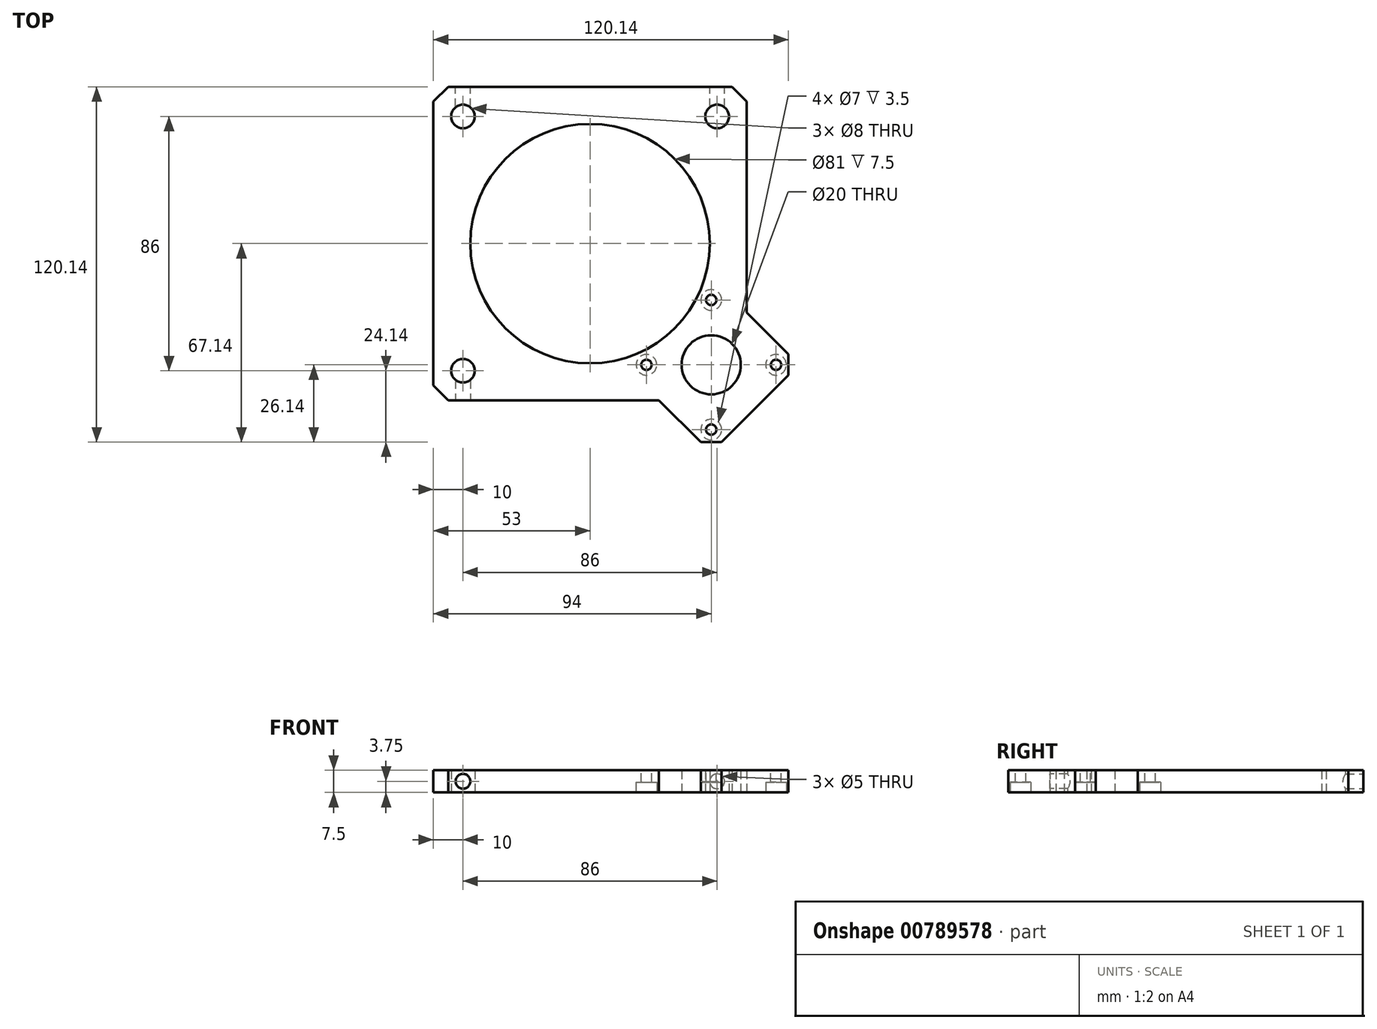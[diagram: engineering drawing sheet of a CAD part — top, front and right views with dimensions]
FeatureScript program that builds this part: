
annotation { "Feature Type Name" : "Feature", "Feature Type Description" : "" }
export const myFeature = defineFeature(function(context is Context, id is Id, definition is map)
    precondition{}
    {
        {
            var Q0;
            Q0=qCreatedBy(makeId("Top.planeOp"),FACE);
            var sketch = newSketch(context, id + "F0", { "sketchPlane" : qUnion([Q0])});
            skPoint(sketch, "E0.middle", {"position": v(0, 0) * mm});
            skCircle(sketch, "E1", {"center": v(0, 0) * mm, "radius": 40.5 * mm});
            skCircle(sketch, "E2", {"center": v(43, 43) * mm, "radius": 4 * mm});
            skCircle(sketch, "E3", {"center": v(-43, -43) * mm, "radius": 4 * mm});
            skLineSegment(sketch, "E4", {"start": v(41, -70.68) * mm, "end": v(41, -41) * mm});
            skCircle(sketch, "E5", {"center": v(41, -41) * mm, "radius": 10 * mm});
            skCircle(sketch, "E6", {"center": v(-43, 43) * mm, "radius": 4 * mm});
            skLineSegment(sketch, "E7", {"start": v(-53, 53) * mm, "end": v(-53, -53) * mm});
            skLineSegment(sketch, "E8", {"start": v(-53, -53) * mm, "end": v(23.32, -53) * mm});
            skLineSegment(sketch, "E9", {"start": v(-53, 53) * mm, "end": v(53, 53) * mm});
            skLineSegment(sketch, "E10", {"start": v(53, 53) * mm, "end": v(53, -23.32) * mm});
            skLineSegment(sketch, "E11", {"start": v(23.32, -53) * mm, "end": v(41, -70.68) * mm});
            skLineSegment(sketch, "E12", {"start": v(53, -23.32) * mm, "end": v(70.68, -41) * mm});
            skLineSegment(sketch, "E13", {"start": v(70.68, -41) * mm, "end": v(41, -70.68) * mm});
            skPoint(sketch, "E14.end.orphan", {"position": v(41, -70.68) * mm});
            skSolve(sketch);
        }
        {
            var Q0;
            Q0=makeQuery(id+"F0.imprint","IMPRINT",FACE,{"disambiguationData":[TD([[makeQuery(id+"F0.imprint","IMPRINT",EDGE,{"derivedFrom":sQuery(id+"F0.wireOp",EDGE,"E1")}),-1.0]])]});
            var Q1;
            {var subQ1=sQuery(id+"F0.wireOp",EDGE,"E0.left");var subQ6=sQuery(id+"F0.wireOp",EDGE,"E0.bottom");var subQ9=makeQuery(id+"F0.imprint","INTERSECT",VERTEX,{"derivedFrom":[subQ6,subQ1]});Q1=makeQuery(id+"F0.imprint","IMPRINT",FACE,{"disambiguationData":[TD([[makeQuery(id+"F0.imprint","IMPRINT",EDGE,{"disambiguationData":[TD([[subQ9,-1.0]])],"derivedFrom":subQ6}),1.0]])]});}
            var Q2;
            {var subQ1=sQuery(id+"F0.wireOp",EDGE,"E0.right");var subQ6=sQuery(id+"F0.wireOp",EDGE,"E0.top");var subQ9=makeQuery(id+"F0.imprint","INTERSECT",VERTEX,{"derivedFrom":[subQ6,subQ1]});Q2=makeQuery(id+"F0.imprint","IMPRINT",FACE,{"disambiguationData":[TD([[makeQuery(id+"F0.imprint","IMPRINT",EDGE,{"disambiguationData":[TD([[subQ9,1.0]])],"derivedFrom":subQ6}),-1.0]])]});}
            var Q3;
            {var subQ1=sQuery(id+"F0.wireOp",EDGE,"E0.right");var subQ6=sQuery(id+"F0.wireOp",EDGE,"E0.bottom");var subQ9=makeQuery(id+"F0.imprint","INTERSECT",VERTEX,{"derivedFrom":[subQ6,subQ1]});Q3=makeQuery(id+"F0.imprint","IMPRINT",FACE,{"disambiguationData":[TD([[makeQuery(id+"F0.imprint","IMPRINT",EDGE,{"disambiguationData":[TD([[subQ9,1.0]])],"derivedFrom":subQ6}),1.0]])]});}
            var Q4;
            {var subQ1=sQuery(id+"F0.wireOp",EDGE,"0d9eabcc-9e13-4dd9-8463-7bf05dad1fff");var subQ11=sQuery(id+"F0.wireOp",EDGE,"E0.bottom");var subQ18=makeQuery(id+"F0.imprint","INTERSECT",VERTEX,{"derivedFrom":[subQ11,subQ1]});Q4=makeQuery(id+"F0.imprint","IMPRINT",FACE,{"disambiguationData":[TD([[makeQuery(id+"F0.imprint","IMPRINT",EDGE,{"disambiguationData":[TD([[subQ18,-1.0]])],"derivedFrom":subQ11}),1.0]])]});}
            var Q5;
            {var subQ0=sQuery(id+"F0.wireOp",EDGE,"E0.left");var subQ1=sQuery(id+"F0.wireOp",EDGE,"E0.top");var subQ2=makeQuery(id+"F0.imprint","INTERSECT",VERTEX,{"derivedFrom":[subQ1,subQ0]});Q5=makeQuery(id+"F0.imprint","IMPRINT",FACE,{"disambiguationData":[TD([[makeQuery(id+"F0.imprint","IMPRINT",EDGE,{"disambiguationData":[TD([[subQ2,-1.0]])],"derivedFrom":subQ1}),-1.0]])]});}
            extrude(context, id + "F1", {"entities" : qUnion([Q0, Q1, Q2, Q3, Q4, Q5]), "depth" : 7.5 * mm, "offsetDistance" : 25 * mm});
        }
        {
            var Q0;
            Q0=makeQuery(id+"F1.opExtrude","CAP_FACE",FACE,{"disambiguationData":[OSD([sQuery(id+"F0.wireOp",EDGE,"E0.bottom"),sQuery(id+"F0.wireOp",EDGE,"E0.top"),sQuery(id+"F0.wireOp",EDGE,"E0.left"),sQuery(id+"F0.wireOp",EDGE,"E0.right"),sQuery(id+"F0.wireOp",EDGE,"E1"),sQuery(id+"F0.wireOp",EDGE,"E2"),sQuery(id+"F0.wireOp",EDGE,"E3"),sQuery(id+"F0.wireOp",EDGE,"E5"),sQuery(id+"F0.wireOp",EDGE,"E6")])],"isStart":false});
            var sketch = newSketch(context, id + "F2", { "sketchPlane" : qUnion([Q0])});
            skPoint(sketch, "E15", {"position": v(41, -41) * mm});
            skPoint(sketch, "E16", {"position": v(41, -19.08) * mm});
            skLineSegment(sketch, "E17", {"start": v(41, -19.08) * mm, "end": v(19.08, -41) * mm});
            skLineSegment(sketch, "E18", {"start": v(41, -41) * mm, "end": v(30.04, -30.04) * mm});
            skLineSegment(sketch, "E19", {"start": v(41, -41) * mm, "end": v(51.96, -51.96) * mm});
            skLineSegment(sketch, "E20", {"start": v(51.96, -51.96) * mm, "end": v(62.92, -41) * mm});
            skLineSegment(sketch, "E21", {"start": v(51.96, -51.96) * mm, "end": v(41, -62.92) * mm});
            skCircle(sketch, "E22", {"center": v(41, -19.08) * mm, "radius": 1.75 * mm});
            skCircle(sketch, "E23", {"center": v(62.92, -41) * mm, "radius": 1.75 * mm});
            skCircle(sketch, "E24", {"center": v(19.08, -41) * mm, "radius": 1.75 * mm});
            skCircle(sketch, "E25", {"center": v(41, -62.92) * mm, "radius": 1.75 * mm});
            skCircle(sketch, "E26", {"center": v(19.08, -41) * mm, "radius": 2.75 * mm});
            skCircle(sketch, "E27", {"center": v(41, -19.08) * mm, "radius": 2.75 * mm});
            skCircle(sketch, "E28", {"center": v(41, -62.92) * mm, "radius": 2.75 * mm});
            skCircle(sketch, "E29", {"center": v(62.92, -41) * mm, "radius": 2.75 * mm});
            skSolve(sketch);
        }
        {
            var Q0;
            Q0=makeQuery(id+"F2.imprint","IMPRINT",FACE,{"disambiguationData":[TD([[makeQuery(id+"F2.imprint","IMPRINT",EDGE,{"derivedFrom":sQuery(id+"F2.wireOp",EDGE,"E22")}),1.0]])]});
            var Q1;
            Q1=makeQuery(id+"F2.imprint","IMPRINT",FACE,{"disambiguationData":[TD([[makeQuery(id+"F2.imprint","IMPRINT",EDGE,{"derivedFrom":sQuery(id+"F2.wireOp",EDGE,"E24")}),1.0]])]});
            var Q2;
            Q2=makeQuery(id+"F2.imprint","IMPRINT",FACE,{"disambiguationData":[TD([[makeQuery(id+"F2.imprint","IMPRINT",EDGE,{"derivedFrom":sQuery(id+"F2.wireOp",EDGE,"E25")}),1.0]])]});
            var Q3;
            Q3=makeQuery(id+"F2.imprint","IMPRINT",FACE,{"disambiguationData":[TD([[makeQuery(id+"F2.imprint","IMPRINT",EDGE,{"derivedFrom":sQuery(id+"F2.wireOp",EDGE,"E23")}),1.0]])]});
            extrude(context, id + "F3", {"entities" : qUnion([Q0, Q1, Q2, Q3]), "operationType" : NewBodyOperationType.REMOVE, "oppositeDirection" : true, "depth" : 25 * mm, "offsetDistance" : 25 * mm});
        }
        {
            var Q0;
            Q0=makeQuery(id+"F1.opExtrude","CAP_FACE",FACE,{"disambiguationData":[OSD([sQuery(id+"F0.wireOp",EDGE,"E0.bottom"),sQuery(id+"F0.wireOp",EDGE,"E0.top"),sQuery(id+"F0.wireOp",EDGE,"E0.left"),sQuery(id+"F0.wireOp",EDGE,"E0.right"),sQuery(id+"F0.wireOp",EDGE,"E1"),sQuery(id+"F0.wireOp",EDGE,"E2"),sQuery(id+"F0.wireOp",EDGE,"E3"),sQuery(id+"F0.wireOp",EDGE,"E5"),sQuery(id+"F0.wireOp",EDGE,"E6")])],"isStart":true});
            var sketch = newSketch(context, id + "F4", { "sketchPlane" : qUnion([Q0])});
            skPoint(sketch, "E30", {"position": v(41, 41) * mm});
            skPoint(sketch, "E31", {"position": v(41, 62.92) * mm});
            skLineSegment(sketch, "E32", {"start": v(41, 62.92) * mm, "end": v(19.08, 41) * mm});
            skLineSegment(sketch, "E33", {"start": v(41, 41) * mm, "end": v(30.04, 51.96) * mm});
            skLineSegment(sketch, "E34", {"start": v(41, 41) * mm, "end": v(51.96, 30.04) * mm});
            skLineSegment(sketch, "E35", {"start": v(51.96, 30.04) * mm, "end": v(62.92, 41) * mm});
            skLineSegment(sketch, "E36", {"start": v(51.96, 30.04) * mm, "end": v(41, 19.08) * mm});
            skCircle(sketch, "E37", {"center": v(41, 62.92) * mm, "radius": 1.75 * mm});
            skCircle(sketch, "E38", {"center": v(62.92, 41) * mm, "radius": 1.75 * mm});
            skCircle(sketch, "E39", {"center": v(19.08, 41) * mm, "radius": 1.75 * mm});
            skCircle(sketch, "E40", {"center": v(41, 19.08) * mm, "radius": 1.75 * mm});
            skCircle(sketch, "E41", {"center": v(19.08, 41) * mm, "radius": 3.5 * mm});
            skCircle(sketch, "E42", {"center": v(41, 62.92) * mm, "radius": 3.5 * mm});
            skCircle(sketch, "E43", {"center": v(41, 19.08) * mm, "radius": 3.5 * mm});
            skCircle(sketch, "E44", {"center": v(62.92, 41) * mm, "radius": 3.5 * mm});
            skSolve(sketch);
        }
        {
            var Q0;
            Q0=makeQuery(id+"F4.imprint","IMPRINT",FACE,{"disambiguationData":[TD([[makeQuery(id+"F4.imprint","IMPRINT",EDGE,{"derivedFrom":sQuery(id+"F4.wireOp",EDGE,"E41")}),1.0]])]});
            var Q1;
            Q1=makeQuery(id+"F4.imprint","IMPRINT",FACE,{"disambiguationData":[TD([[makeQuery(id+"F4.imprint","IMPRINT",EDGE,{"derivedFrom":sQuery(id+"F4.wireOp",EDGE,"E42")}),1.0]])]});
            var Q2;
            Q2=makeQuery(id+"F4.imprint","IMPRINT",FACE,{"disambiguationData":[TD([[makeQuery(id+"F4.imprint","IMPRINT",EDGE,{"derivedFrom":sQuery(id+"F4.wireOp",EDGE,"E44")}),1.0]])]});
            var Q3;
            Q3=makeQuery(id+"F4.imprint","IMPRINT",FACE,{"disambiguationData":[TD([[makeQuery(id+"F4.imprint","IMPRINT",EDGE,{"derivedFrom":sQuery(id+"F4.wireOp",EDGE,"E40")}),1.0]])]});
            extrude(context, id + "F5", {"entities" : qUnion([Q0, Q1, Q2, Q3]), "operationType" : NewBodyOperationType.REMOVE, "oppositeDirection" : true, "depth" : 3.5 * mm, "offsetDistance" : 25 * mm});
        }
        {
            var Q0;
            Q0=makeQuery(id+"F1.opExtrude","SWEPT_FACE",FACE,{"disambiguationData":[OSD([sQuery(id+"F0.wireOp",EDGE,"E9")])]});
            var sketch = newSketch(context, id + "F6", { "sketchPlane" : qUnion([Q0])});
            skPoint(sketch, "E45", {"position": v(-43, 3.75) * mm});
            skPoint(sketch, "E45.positionSnap0", {"position": v(-53, 3.75) * mm});
            skPoint(sketch, "E46", {"position": v(43, 3.75) * mm});
            skPoint(sketch, "E46.positionSnap0", {"position": v(53, 3.75) * mm});
            skCircle(sketch, "E47", {"center": v(-43, 3.75) * mm, "radius": 2.5 * mm});
            skCircle(sketch, "E48", {"center": v(43, 3.75) * mm, "radius": 2.5 * mm});
            skSolve(sketch);
        }
        {
            var Q0;
            Q0=makeQuery(id+"F6.imprint","IMPRINT",FACE,{"disambiguationData":[TD([[makeQuery(id+"F6.imprint","IMPRINT",EDGE,{"derivedFrom":sQuery(id+"F6.wireOp",EDGE,"E47")}),1.0]])]});
            var Q1;
            Q1=makeQuery(id+"F6.imprint","IMPRINT",FACE,{"disambiguationData":[TD([[makeQuery(id+"F6.imprint","IMPRINT",EDGE,{"derivedFrom":sQuery(id+"F6.wireOp",EDGE,"E48")}),1.0]])]});
            extrude(context, id + "F7", {"entities" : qUnion([Q0, Q1]), "operationType" : NewBodyOperationType.REMOVE, "oppositeDirection" : true, "depth" : 10 * mm, "offsetDistance" : 25 * mm});
        }
        {
            var Q0;
            Q0=makeQuery(id+"F1.opExtrude","SWEPT_FACE",FACE,{"disambiguationData":[OSD([sQuery(id+"F0.wireOp",EDGE,"E8")])]});
            var sketch = newSketch(context, id + "F8", { "sketchPlane" : qUnion([Q0])});
            skPoint(sketch, "E49", {"position": v(-43, 3.75) * mm});
            skPoint(sketch, "E49.positionSnap0", {"position": v(-53, 3.75) * mm});
            skCircle(sketch, "E50", {"center": v(-43, 3.75) * mm, "radius": 2.5 * mm});
            skSolve(sketch);
        }
        {
            var Q0;
            Q0=makeQuery(id+"F8.imprint","IMPRINT",FACE,{"disambiguationData":[TD([[makeQuery(id+"F8.imprint","IMPRINT",EDGE,{"derivedFrom":sQuery(id+"F8.wireOp",EDGE,"E50")}),1.0]])]});
            extrude(context, id + "F9", {"entities" : qUnion([Q0]), "operationType" : NewBodyOperationType.REMOVE, "oppositeDirection" : true, "depth" : 10 * mm, "offsetDistance" : 25 * mm});
        }
        {
            var Q0;
            Q0=makeQuery(id+"F1.opExtrude","SWEPT_EDGE",EDGE,{"disambiguationData":[OSD([sQuery(id+"F0.wireOp",EDGE,"E12"),sQuery(id+"F0.wireOp",EDGE,"E13")])]});
            var Q1;
            Q1=makeQuery(id+"F1.opExtrude","SWEPT_EDGE",EDGE,{"disambiguationData":[OSD([sQuery(id+"F0.wireOp",EDGE,"E11"),sQuery(id+"F0.wireOp",EDGE,"E13")])]});
            var Q2;
            Q2=makeQuery(id+"F1.opExtrude","SWEPT_EDGE",EDGE,{"disambiguationData":[OSD([sQuery(id+"F0.wireOp",EDGE,"E9"),sQuery(id+"F0.wireOp",EDGE,"E10")])]});
            var Q3;
            Q3=makeQuery(id+"F1.opExtrude","SWEPT_EDGE",EDGE,{"disambiguationData":[OSD([sQuery(id+"F0.wireOp",EDGE,"E7"),sQuery(id+"F0.wireOp",EDGE,"E9")])]});
            var Q4;
            Q4=makeQuery(id+"F1.opExtrude","SWEPT_EDGE",EDGE,{"disambiguationData":[OSD([sQuery(id+"F0.wireOp",EDGE,"E7"),sQuery(id+"F0.wireOp",EDGE,"E8")])]});
            chamfer(context, id + "F10", {"entities" : qUnion([Q0, Q1, Q2, Q3, Q4]), "width" : 5 * mm, "tangentPropagation" : true});
        }
    });
